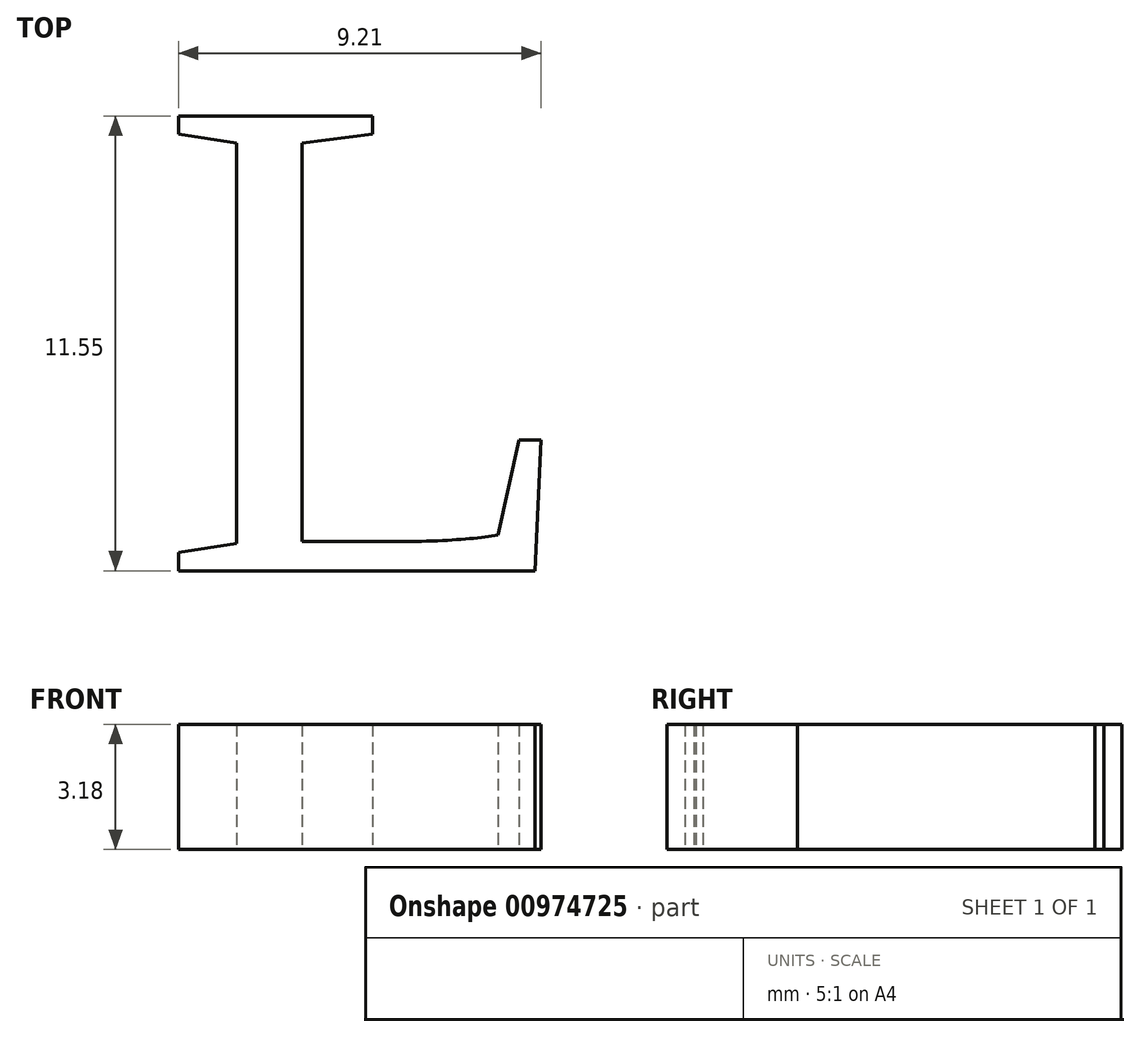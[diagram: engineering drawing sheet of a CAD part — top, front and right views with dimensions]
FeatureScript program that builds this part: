
annotation { "Feature Type Name" : "Feature", "Feature Type Description" : "" }
export const myFeature = defineFeature(function(context is Context, id is Id, definition is map)
    precondition{}
    {
        {
            var Q0;
            Q0=qCreatedBy(makeId("Top.planeOp"),FACE);
            var sketch = newSketch(context, id + "F0", { "sketchPlane" : qUnion([Q0])});
            skText(sketch, "E0", { "text": "L", "fontName": "Tinos-Regular.ttf"});
            const initialGuessF0  = {"E0": [-0.0728, 0.05863, 1, 0, 0.0127]};
            skSetInitialGuess(sketch, initialGuessF0);
            skSolve(sketch);
        }
        {
            var Q0;
            Q0=makeQuery(id+"F0.imprint","IMPRINT",FACE,{"disambiguationData":[TD([[makeQuery(id+"F0.imprint","IMPRINT",EDGE,{"derivedFrom":sQuery(id+"F0.wireOp",EDGE,"E0.sketch_text.stroke-0")}),-1.0]])]});
            extrude(context, id + "F1", {"entities" : qUnion([Q0]), "depth" : 3.17 * mm, "offsetDistance" : 25.4 * mm});
        }
    });
